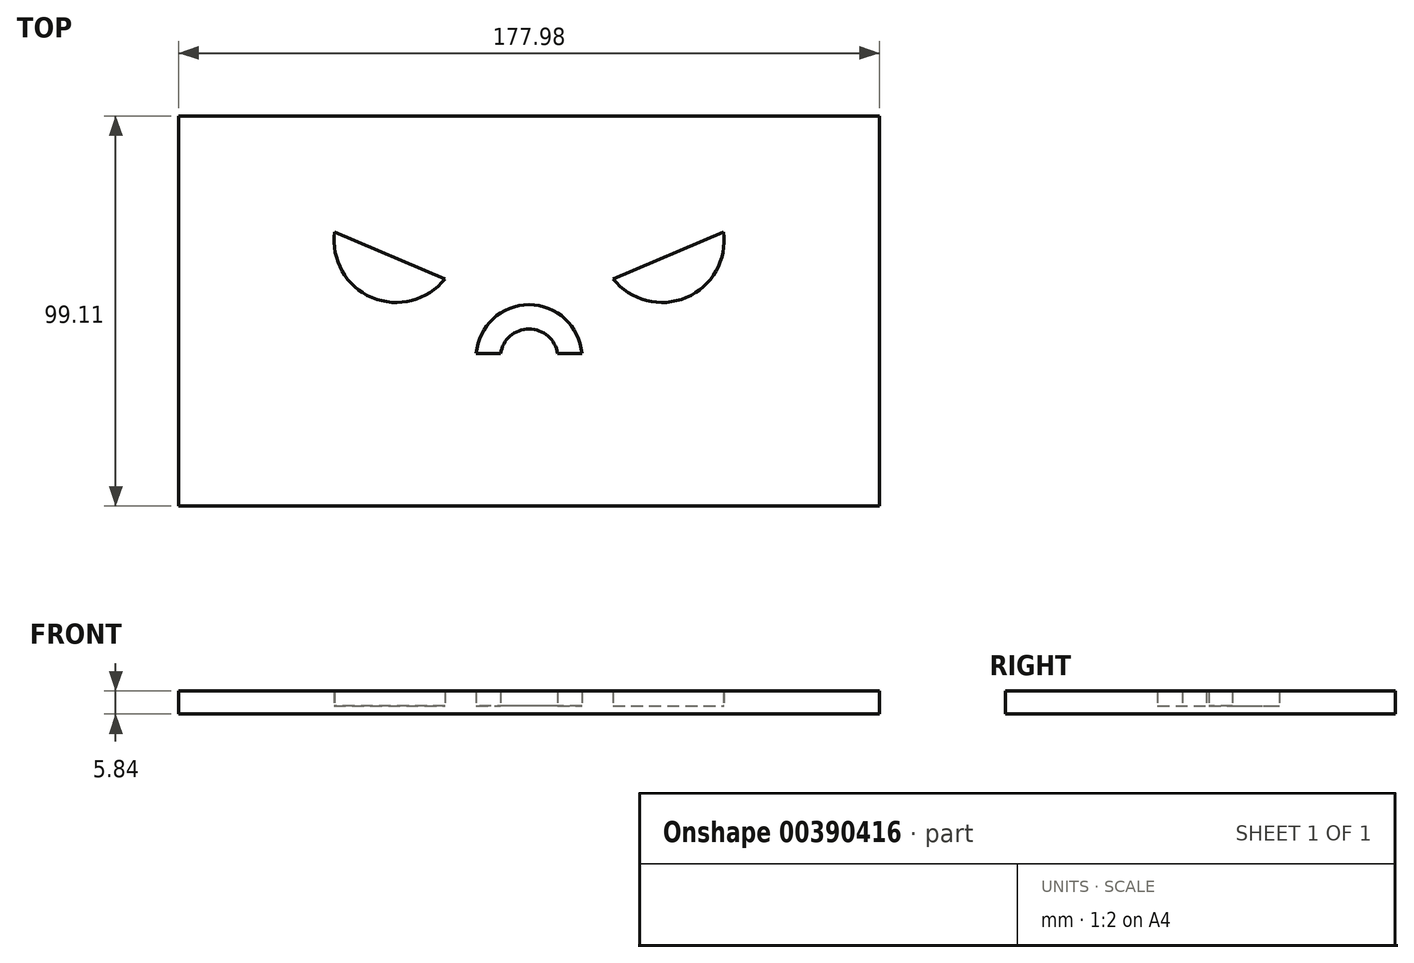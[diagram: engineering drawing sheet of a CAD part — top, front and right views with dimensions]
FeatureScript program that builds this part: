
annotation { "Feature Type Name" : "Feature", "Feature Type Description" : "" }
export const myFeature = defineFeature(function(context is Context, id is Id, definition is map)
    precondition{}
    {
        {
            var Q0;
            Q0=qCreatedBy(makeId("Top.planeOp"),FACE);
            var sketch = newSketch(context, id + "F0", { "sketchPlane" : qUnion([Q0])});
            skPoint(sketch, "E0", {"position": v(0.18, 5.26) * mm});
            skLineSegment(sketch, "E1.bottom", {"start": v(0, 0) * mm, "end": v(177.98, 0) * mm});
            skLineSegment(sketch, "E1.top", {"start": v(0, 99.11) * mm, "end": v(177.98, 99.11) * mm});
            skLineSegment(sketch, "E1.left", {"start": v(0, 0) * mm, "end": v(0, 99.11) * mm});
            skLineSegment(sketch, "E1.right", {"start": v(177.98, 0) * mm, "end": v(177.98, 99.11) * mm});
            skLineSegment(sketch, "E2", {"start": v(67.66, 57.73) * mm, "end": v(39.57, 69.63) * mm});
            skArc(sketch, "E3", {"start": v(102.4, 38.68) * mm, "mid": v(89, 51.13) * mm, "end": v(75.58, 38.68) * mm});
            skArc(sketch, "E4", {"start": v(96.22, 38.68) * mm, "mid": v(89, 44.98) * mm, "end": v(81.76, 38.68) * mm});
            skArc(sketch, "E5", {"start": v(39.57, 69.63) * mm, "mid": v(49.08, 52.97) * mm, "end": v(67.66, 57.73) * mm});
            skLineSegment(sketch, "E6", {"start": v(89, 0) * mm, "end": v(89, 99.11) * mm, "construction": true});
            skLineSegment(sketch, "E7", {"start": v(75.58, 38.68) * mm, "end": v(81.76, 38.68) * mm});
            skLineSegment(sketch, "E8", {"start": v(96.22, 38.68) * mm, "end": v(102.4, 38.68) * mm});
            skLineSegment(sketch, "E9.MirrorCS", {"start": v(110.32, 57.73) * mm, "end": v(138.4, 69.63) * mm});
            skArc(sketch, "E10.MirrorCS", {"start": v(138.4, 69.63) * mm, "mid": v(128.9, 52.97) * mm, "end": v(110.32, 57.73) * mm});
            skSolve(sketch);
        }
        {
            var Q0;
            Q0 = qSketchRegion(id + "F0", true);
            extrude(context, id + "F1", {"entities" : qUnion([Q0]), "depth" : 3.8 * mm});
        }
        {
            var Q0;
            Q0=makeQuery(id+"F1.opExtrude","CAP_FACE",FACE,{"disambiguationData":[OSD([sQuery(id+"F0.wireOp",EDGE,"E1.bottom"),sQuery(id+"F0.wireOp",EDGE,"E1.top"),sQuery(id+"F0.wireOp",EDGE,"E1.left"),sQuery(id+"F0.wireOp",EDGE,"E1.right"),sQuery(id+"F0.wireOp",EDGE,"E2"),sQuery(id+"F0.wireOp",EDGE,"E3"),sQuery(id+"F0.wireOp",EDGE,"E4"),sQuery(id+"F0.wireOp",EDGE,"E5"),sQuery(id+"F0.wireOp",EDGE,"E7"),sQuery(id+"F0.wireOp",EDGE,"E8"),sQuery(id+"F0.wireOp",EDGE,"E9.MirrorCS"),sQuery(id+"F0.wireOp",EDGE,"E10.MirrorCS")])],"isStart":true});
            var sketch = newSketch(context, id + "F2", { "sketchPlane" : qUnion([Q0])});
            skLineSegment(sketch, "E11.bottom", {"start": v(0, 0) * mm, "end": v(177.98, 0) * mm});
            skLineSegment(sketch, "E11.top", {"start": v(0, -99.11) * mm, "end": v(177.98, -99.11) * mm});
            skLineSegment(sketch, "E11.left", {"start": v(0, 0) * mm, "end": v(0, -99.11) * mm});
            skLineSegment(sketch, "E11.right", {"start": v(177.98, 0) * mm, "end": v(177.98, -99.11) * mm});
            skSolve(sketch);
        }
        {
            var Q0;
            Q0 = qSketchRegion(id + "F2", true);
            extrude(context, id + "F3", {"entities" : qUnion([Q0]), "operationType" : NewBodyOperationType.ADD, "depth" : 2.03 * mm});
        }
    });
